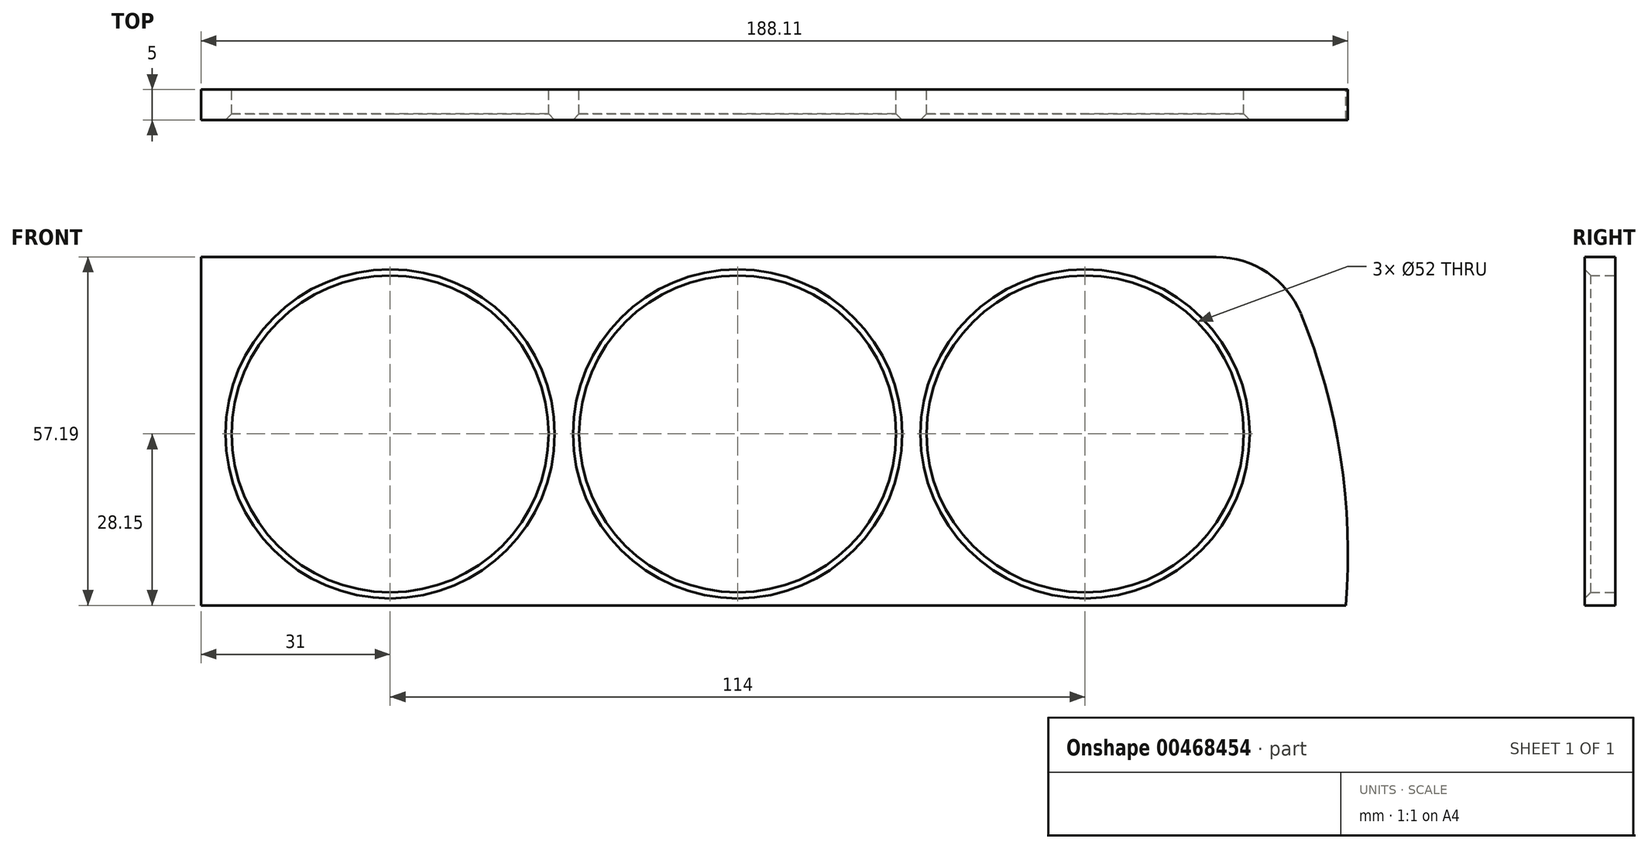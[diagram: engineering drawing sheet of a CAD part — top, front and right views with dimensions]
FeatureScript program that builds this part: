
annotation { "Feature Type Name" : "Feature", "Feature Type Description" : "" }
export const myFeature = defineFeature(function(context is Context, id is Id, definition is map)
    precondition{}
    {
        {
            var Q0;
            Q0=qCreatedBy(makeId("Front.planeOp"),FACE);
            var sketch = newSketch(context, id + "F0", { "sketchPlane" : qUnion([Q0])});
            skLineSegment(sketch, "E0.bottom", {"start": v(-88, 29.04) * mm, "end": v(88, 29.04) * mm});
            skLineSegment(sketch, "E0.top", {"start": v(-88, -28.15) * mm, "end": v(88, -28.15) * mm});
            skLineSegment(sketch, "E0.left", {"start": v(-88, 29.04) * mm, "end": v(-88, -28.15) * mm});
            skLineSegment(sketch, "E0.right", {"start": v(88, 29.04) * mm, "end": v(88, -28.15) * mm});
            skCircle(sketch, "E1", {"center": v(-57, 0) * mm, "radius": 26 * mm});
            skCircle(sketch, "E2", {"center": v(0, 0) * mm, "radius": 26 * mm});
            skCircle(sketch, "E3", {"center": v(57, 0) * mm, "radius": 26 * mm});
            skLineSegment(sketch, "E4", {"start": v(88, -28.15) * mm, "end": v(99.75, -28.15) * mm});
            skArc(sketch, "E5", {"start": v(99.75, -28.15) * mm, "mid": v(98, 1.3) * mm, "end": v(88, 29.04) * mm});
            skSolve(sketch);
        }
        {
            var Q0;
            Q0 = qSketchRegion(id + "F0", true);
            extrude(context, id + "F1", {"entities" : qUnion([Q0]), "depth" : 5 * mm});
        }
        {
            var Q0;
            Q0=makeQuery(id+"F1.opExtrude","SWEPT_EDGE",EDGE,{"disambiguationData":[OSD([sQuery(id+"F0.wireOp",EDGE,"E0.bottom"),sQuery(id+"F0.wireOp",EDGE,"E0.right"),sQuery(id+"F0.wireOp",EDGE,"E5")])]});
            fillet(context, id + "F2", {"entities" : qUnion([Q0]), "radius" : 15 * mm, "tangentPropagation" : true, "allowEdgeOverflow" : false});
        }
        {
            var Q0;
            Q0=makeQuery(id+"F1.opExtrude","CAP_EDGE",EDGE,{"disambiguationData":[OSD([sQuery(id+"F0.wireOp",EDGE,"E1")])],"isStart":false});
            var Q1;
            Q1=makeQuery(id+"F1.opExtrude","CAP_EDGE",EDGE,{"disambiguationData":[OSD([sQuery(id+"F0.wireOp",EDGE,"E2")])],"isStart":false});
            var Q2;
            Q2=makeQuery(id+"F1.opExtrude","CAP_EDGE",EDGE,{"disambiguationData":[OSD([sQuery(id+"F0.wireOp",EDGE,"E3")])],"isStart":false});
            chamfer(context, id + "F3", {"entities" : qUnion([Q0, Q1, Q2]), "width" : 1 * mm, "tangentPropagation" : true});
        }
    });
